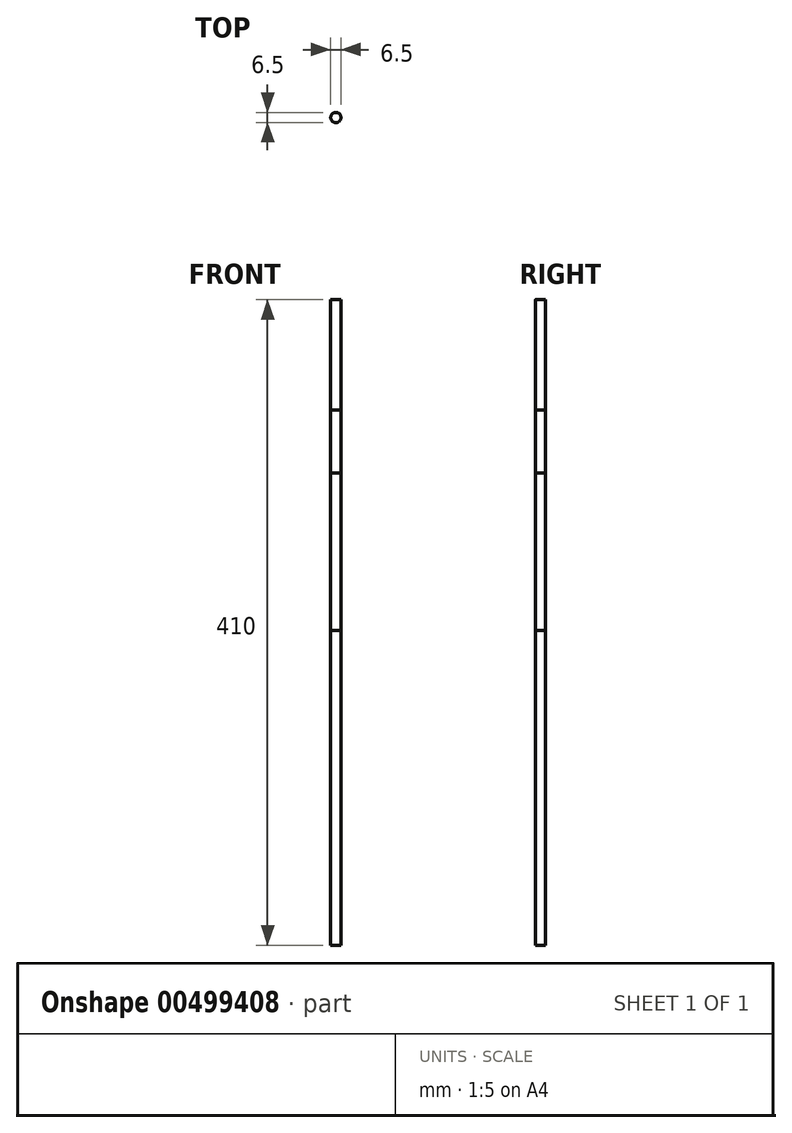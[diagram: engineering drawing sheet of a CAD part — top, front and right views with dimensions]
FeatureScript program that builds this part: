
annotation { "Feature Type Name" : "Feature", "Feature Type Description" : "" }
export const myFeature = defineFeature(function(context is Context, id is Id, definition is map)
    precondition{}
    {
        {
            var Q0;
            Q0=qCreatedBy(makeId("Top.planeOp"),FACE);
            var sketch = newSketch(context, id + "F0", { "sketchPlane" : qUnion([Q0])});
            skCircle(sketch, "E0", {"center": v(0, 0) * mm, "radius": 3.25 * mm});
            skSolve(sketch);
        }
        {
            var Q0;
            Q0=makeQuery(id+"F0.imprint","IMPRINT",FACE,{"disambiguationData":[TD([[makeQuery(id+"F0.imprint","IMPRINT",EDGE,{"derivedFrom":sQuery(id+"F0.wireOp",EDGE,"E0")}),1.0]])]});
            extrude(context, id + "F1", {"entities" : qUnion([Q0]), "depth" : 200 * mm, "offsetDistance" : 25 * mm});
        }
        {
            var Q0;
            Q0=makeQuery(id+"F1.opExtrude","CAP_FACE",FACE,{"disambiguationData":[OSD([sQuery(id+"F0.wireOp",EDGE,"E0")])],"isStart":false});
            extrude(context, id + "F2", {"entities" : qUnion([Q0]), "depth" : 100 * mm, "offsetDistance" : 25 * mm});
        }
        {
            var Q0;
            Q0=makeQuery(id+"F1.opExtrude","CAP_FACE",FACE,{"disambiguationData":[OSD([sQuery(id+"F0.wireOp",EDGE,"E0")])],"isStart":false});
            extrude(context, id + "F3", {"entities" : qUnion([Q0]), "depth" : 140 * mm, "offsetDistance" : 25 * mm});
        }
        {
            var Q0;
            Q0=makeQuery(id+"F3.opExtrude","CAP_FACE",FACE,{"disambiguationData":[OSD([sQuery(id+"F0.wireOp",EDGE,"E0")])],"isStart":false});
            extrude(context, id + "F4", {"entities" : qUnion([Q0]), "depth" : 70 * mm, "offsetDistance" : 25 * mm});
        }
    });
